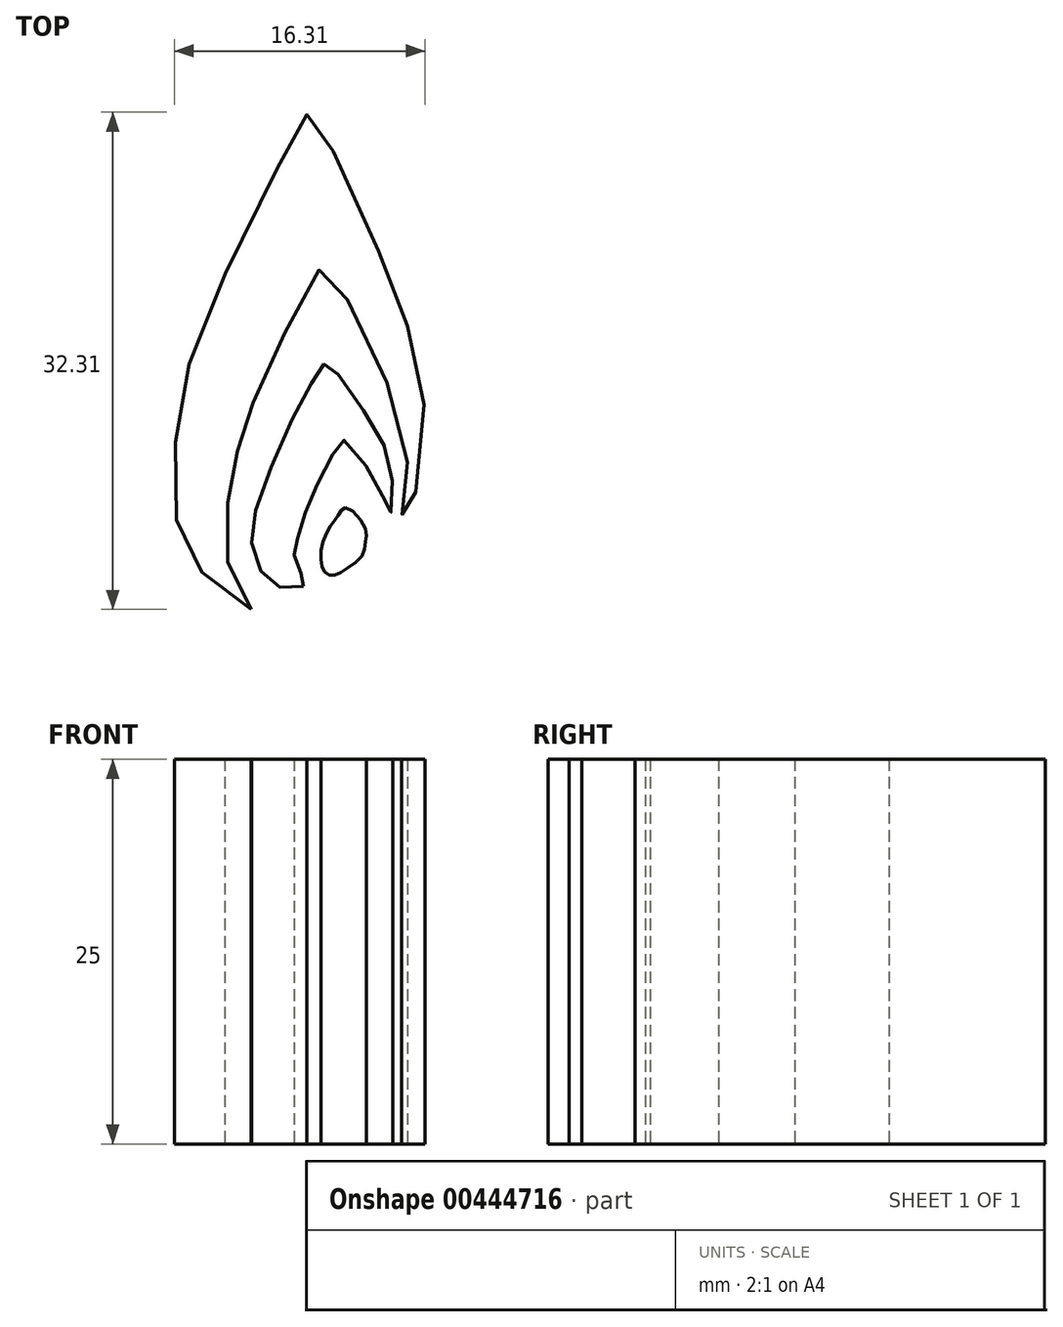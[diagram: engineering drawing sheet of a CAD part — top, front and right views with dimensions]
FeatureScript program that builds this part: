
annotation { "Feature Type Name" : "Feature", "Feature Type Description" : "" }
export const myFeature = defineFeature(function(context is Context, id is Id, definition is map)
    precondition{}
    {
        {
            var Q0;
            Q0=qCreatedBy(makeId("Top.planeOp"),FACE);
            var sketch = newSketch(context, id + "F0", { "sketchPlane" : qUnion([Q0])});
            skFitSpline(sketch, "E0", {"points": [v(-98.48, 13.73) * mm, v(-101.81, 16.25) * mm, v(-103.32, 19.53) * mm, v(-103.22, 26.24) * mm, v(-101, 33.66) * mm, v(-95.5, 44.8) * mm, v(-94.77, 45.97) * mm, v(-94.57, 46) * mm, v(-90.57, 37.88) * mm, v(-88.03, 31.15) * mm, v(-87.3, 23.5) * mm, v(-88.62, 19.37) * mm, v(-88.58, 20.68) * mm, v(-88.4, 24.05) * mm, v(-91.4, 32.37) * mm, v(-93.71, 35.82) * mm, v(-94.16, 35.68) * mm, v(-97.25, 29.6) * mm, v(-98.85, 25.8) * mm, v(-99.55, 23.16) * mm, v(-100.06, 20.06) * mm, v(-99.77, 16.15) * mm, v(-98.48, 13.73) * mm]});
            skSolve(sketch);
        }
        {
            var Q0;
            Q0=makeQuery(id+"F0.imprint","IMPRINT",FACE,{"disambiguationData":[TD([[makeQuery(id+"F0.imprint","IMPRINT",EDGE,{"derivedFrom":sQuery(id+"F0.wireOp",EDGE,"E0")}),-1.0]])]});
            extrude(context, id + "F1", {"entities" : qUnion([Q0]), "depth" : 25 * mm});
        }
        {
            var Q0;
            Q0=qCreatedBy(makeId("Top.planeOp"),FACE);
            var sketch = newSketch(context, id + "F2", { "sketchPlane" : qUnion([Q0])});
            skFitSpline(sketch, "E1", {"points": [v(-95.07, 15.22) * mm, v(-96.46, 15.13) * mm, v(-97.67, 15.97) * mm, v(-98.43, 17.97) * mm, v(-97.96, 20.8) * mm, v(-95.53, 26.6) * mm, v(-94.08, 29.17) * mm, v(-93.62, 29.72) * mm, v(-93.13, 29.38) * mm, v(-90.52, 25.67) * mm, v(-89.36, 22.69) * mm, v(-89.4, 20.02) * mm, v(-89.68, 20.46) * mm, v(-90.6, 22.43) * mm, v(-92.46, 24.74) * mm, v(-92.64, 24.74) * mm, v(-93.77, 22.63) * mm, v(-94.72, 20.66) * mm, v(-95.42, 18.46) * mm, v(-95.5, 18.11) * mm, v(-95.68, 17.19) * mm, v(-95.47, 16.43) * mm, v(-94.84, 15.4) * mm, v(-95.07, 15.22) * mm]});
            skSolve(sketch);
        }
        {
            var Q0;
            Q0=makeQuery(id+"F2.imprint","IMPRINT",FACE,{"disambiguationData":[TD([[makeQuery(id+"F2.imprint","IMPRINT",EDGE,{"derivedFrom":sQuery(id+"F2.wireOp",EDGE,"E1")}),-1.0]])]});
            extrude(context, id + "F3", {"entities" : qUnion([Q0]), "depth" : 25 * mm});
        }
        {
            var Q0;
            Q0=qCreatedBy(makeId("Top.planeOp"),FACE);
            var sketch = newSketch(context, id + "F4", { "sketchPlane" : qUnion([Q0])});
            skFitSpline(sketch, "E2", {"points": [v(-92.35, 20.34) * mm, v(-92.7, 20) * mm, v(-93.13, 19.42) * mm, v(-93.74, 18.32) * mm, v(-93.94, 16.9) * mm, v(-93.7, 16.17) * mm, v(-93.21, 15.91) * mm, v(-92.43, 16.26) * mm, v(-91.25, 17.21) * mm, v(-91.04, 18.2) * mm, v(-91.07, 19.07) * mm, v(-92.35, 20.34) * mm]});
            skSolve(sketch);
        }
        {
            var Q0;
            Q0 = qSketchRegion(id + "F4", true);
            extrude(context, id + "F5", {"entities" : qUnion([Q0]), "depth" : 25 * mm});
        }
    });
